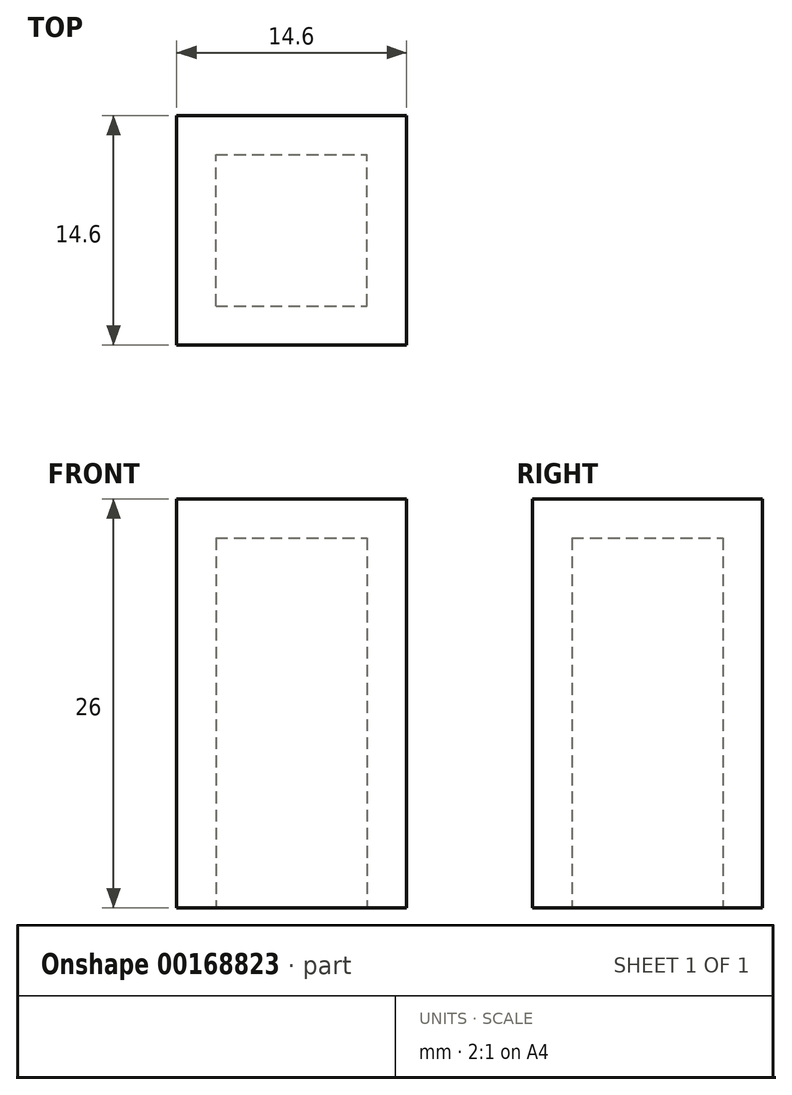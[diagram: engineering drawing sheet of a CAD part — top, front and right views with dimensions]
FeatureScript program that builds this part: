
annotation { "Feature Type Name" : "Feature", "Feature Type Description" : "" }
export const myFeature = defineFeature(function(context is Context, id is Id, definition is map)
    precondition{}
    {
        {
            var Q0;
            Q0=qCreatedBy(makeId("Front.planeOp"),FACE);
            var sketch = newSketch(context, id + "F0", { "sketchPlane" : qUnion([Q0])});
            skLineSegment(sketch, "E0.bottom", {"start": v(-7.3, 13) * mm, "end": v(7.3, 13) * mm});
            skLineSegment(sketch, "E0.top", {"start": v(-7.3, -13) * mm, "end": v(7.3, -13) * mm});
            skLineSegment(sketch, "E0.left", {"start": v(-7.3, 13) * mm, "end": v(-7.3, -13) * mm});
            skLineSegment(sketch, "E0.right", {"start": v(7.3, 13) * mm, "end": v(7.3, -13) * mm});
            skPoint(sketch, "E0.middle", {"position": v(0, 0) * mm});
            skSolve(sketch);
        }
        {
            var Q0;
            Q0 = qSketchRegion(id + "F0", true);
            extrude(context, id + "F1", {"entities" : qUnion([Q0]), "depth" : 14.6 * mm});
        }
        {
            var Q0;
            Q0=makeQuery(id+"F1.opExtrude","SWEPT_FACE",FACE,{"disambiguationData":[OSD([sQuery(id+"F0.wireOp",EDGE,"E0.top")])]});
            shell(context, id + "F2", {"entities" : qUnion([Q0]), "thickness" : 2.5 * mm});
        }
    });
